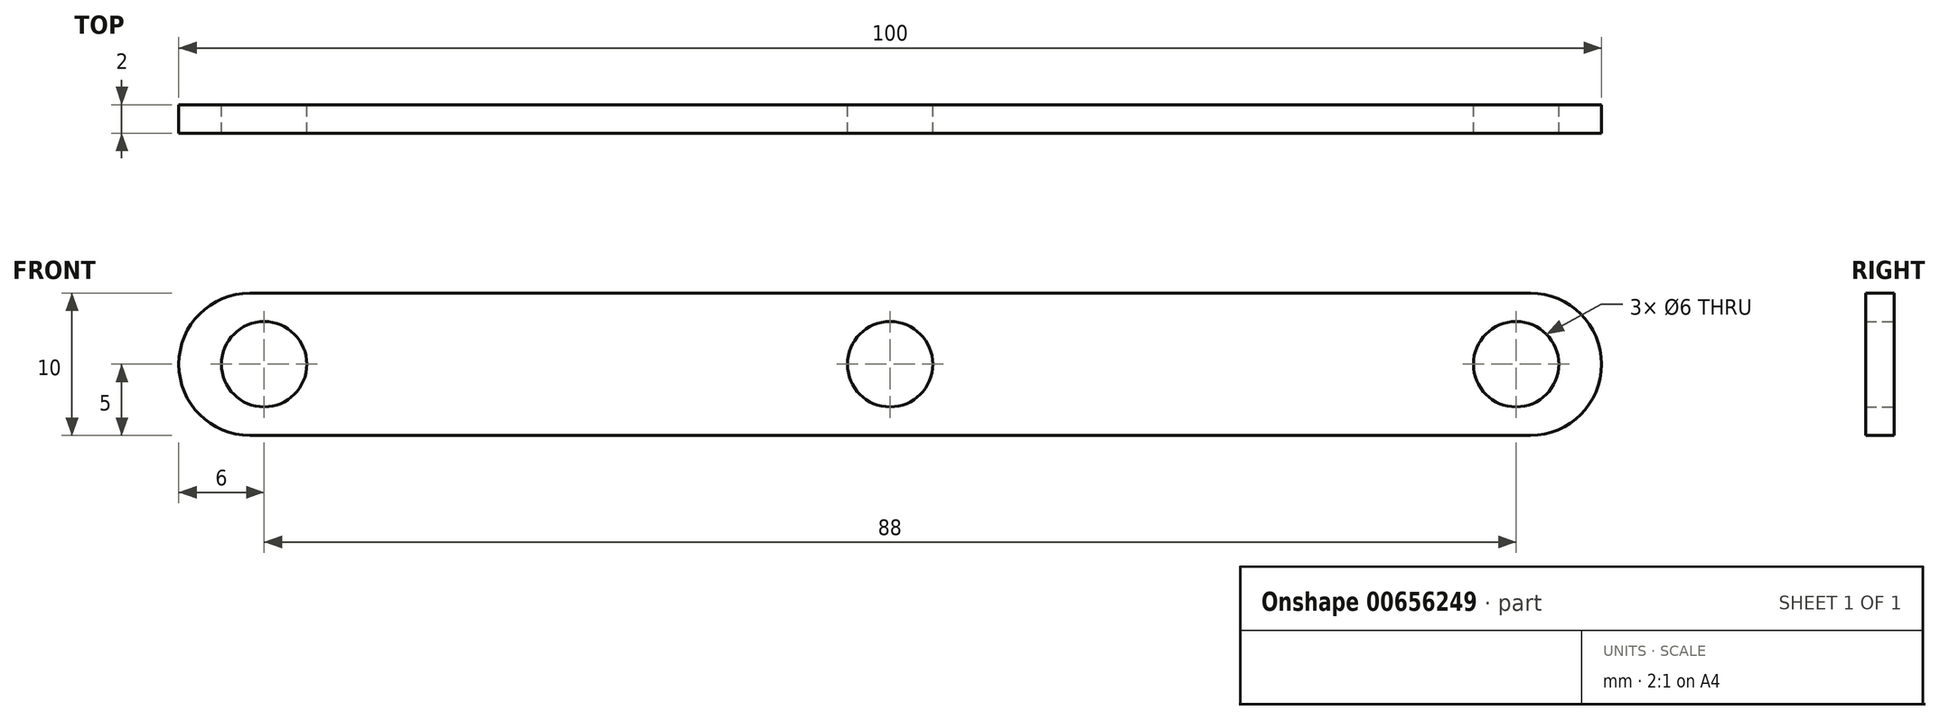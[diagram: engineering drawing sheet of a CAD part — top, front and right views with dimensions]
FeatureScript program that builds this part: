
annotation { "Feature Type Name" : "Feature", "Feature Type Description" : "" }
export const myFeature = defineFeature(function(context is Context, id is Id, definition is map)
    precondition{}
    {
        {
            var Q0;
            Q0=qCreatedBy(makeId("Front.planeOp"),FACE);
            var sketch = newSketch(context, id + "F0", { "sketchPlane" : qUnion([Q0])});
            skLineSegment(sketch, "E0.bottom", {"start": v(-50, 5) * mm, "end": v(50, 5) * mm});
            skLineSegment(sketch, "E0.top", {"start": v(-50, -5) * mm, "end": v(50, -5) * mm});
            skLineSegment(sketch, "E0.left", {"start": v(-50, 5) * mm, "end": v(-50, -5) * mm});
            skLineSegment(sketch, "E0.right", {"start": v(50, 5) * mm, "end": v(50, -5) * mm});
            skCircle(sketch, "E1", {"center": v(0, 0) * mm, "radius": 3 * mm});
            skCircle(sketch, "E2", {"center": v(-44, 0) * mm, "radius": 3 * mm});
            skPoint(sketch, "E2.centerSnap0", {"position": v(-50, 0) * mm});
            skCircle(sketch, "E3", {"center": v(44, 0) * mm, "radius": 3 * mm});
            skSolve(sketch);
        }
        {
            var Q0;
            Q0 = qSketchRegion(id + "F0", true);
            extrude(context, id + "F1", {"entities" : qUnion([Q0]), "depth" : 2 * mm, "offsetDistance" : 25 * mm});
        }
        {
            var Q0;
            Q0=makeQuery(id+"F1.opExtrude","SWEPT_EDGE",EDGE,{"disambiguationData":[OSD([sQuery(id+"F0.wireOp",EDGE,"E0.bottom"),sQuery(id+"F0.wireOp",EDGE,"E0.left")])]});
            var Q1;
            Q1=makeQuery(id+"F1.opExtrude","SWEPT_EDGE",EDGE,{"disambiguationData":[OSD([sQuery(id+"F0.wireOp",EDGE,"E0.top"),sQuery(id+"F0.wireOp",EDGE,"E0.left")])]});
            var Q2;
            Q2=makeQuery(id+"F1.opExtrude","SWEPT_EDGE",EDGE,{"disambiguationData":[OSD([sQuery(id+"F0.wireOp",EDGE,"E0.bottom"),sQuery(id+"F0.wireOp",EDGE,"E0.right")])]});
            var Q3;
            Q3=makeQuery(id+"F1.opExtrude","SWEPT_EDGE",EDGE,{"disambiguationData":[OSD([sQuery(id+"F0.wireOp",EDGE,"E0.top"),sQuery(id+"F0.wireOp",EDGE,"E0.right")])]});
            fillet(context, id + "F2", {"entities" : qUnion([Q0, Q1, Q2, Q3]), "radius" : 5 * mm, "tangentPropagation" : true, "allowEdgeOverflow" : false});
        }
    });
